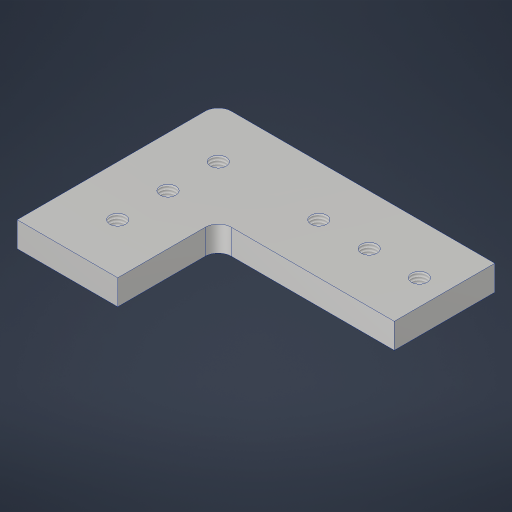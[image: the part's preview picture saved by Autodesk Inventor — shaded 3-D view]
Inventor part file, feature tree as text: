
AUTODESK INVENTOR PART (.ipt)
format: ipt  version: 2023.4 (Build 274418000, 418)  size: 259,072 bytes
history: native  units: in
note: dims shown in document units (in); Inventor stores cm internally (conversion verified against a paired STEP export)
features: sketch x3, extrude x2, hole x1, fillet x1
ambient origin geometry x8: Origin, YZ Plane, XZ Plane, XY Plane, X Axis, Y Axis, Z Axis, Center Point
bodies: Solid1 (feature_tree)
feature tree (7):
  extrude  "Extrusion1"  Depth=2.0in
  extrude  "Extrusion2"  Depth=1.0in
  hole  "Hole2"  [1 undecoded]
  fillet  "Fillet1"  Radius=0.5in
  sketch  "Sketch1"  dims[d0=1.0in d1=2.0in]
  sketch  "Sketch3"  dims[d2=0.25in d3=0.0in d14=1.0in]
  sketch  "Sketch4"  dims[d15=1.75in d16=0.0in d17=0.5in d18=0.5in d19=0.5in d20=1.0in d21=0.5in d22=0.5in d23=0.156in d24=0.38in d25=0.375in d26=0.25in d27=0.5635in d28=1.0in d29=0.8108in d30=0.13in]
note: 1 required parameter value undecoded (feature->parameter linkage not recoverable at this tier; creation-order binding heuristic only, values carry confidence <= 0.55)
